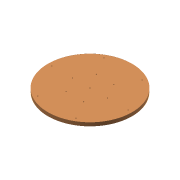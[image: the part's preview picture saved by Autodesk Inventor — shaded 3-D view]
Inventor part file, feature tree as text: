
AUTODESK INVENTOR PART (.ipt)
format: ipt  version: 2016 (Build 200138000, 138)  size: 156,160 bytes
history: native  units: in
note: dims shown in document units (in); Inventor stores cm internally (conversion verified against a paired STEP export)
features: sketch x2, extrude x1, hole x1, pattern_circular x1
ambient origin geometry x8: Origin, YZ Plane, XZ Plane, XY Plane, X Axis, Y Axis, Z Axis, Center Point
bodies: Solid1 (feature_tree)
feature tree (5):
  extrude  "Extrusion1"  Depth=1.0in TaperAngle=0.0deg
  hole  "Hole1"  [1 undecoded]
  pattern_circular  "Circular Pattern1"  Count=6 Angle=360.0deg
  sketch  "Sketch1"  dims[d0=24.0157in d1=1.0in d2=0.0in]
  sketch  "Sketch2"  dims[d3=5.0in d4=5.9055in d5=0.25in d6=0.75in d7=0.375in d8=0.25in d9=0.5635in d10=1.0in d11=0.8108in d12=2.3622in d13=360.0deg d15=0.3543in d16=0.3543in d17=0.3543in]
note: 1 required parameter value undecoded (feature->parameter linkage not recoverable at this tier; creation-order binding heuristic only, values carry confidence <= 0.55)
